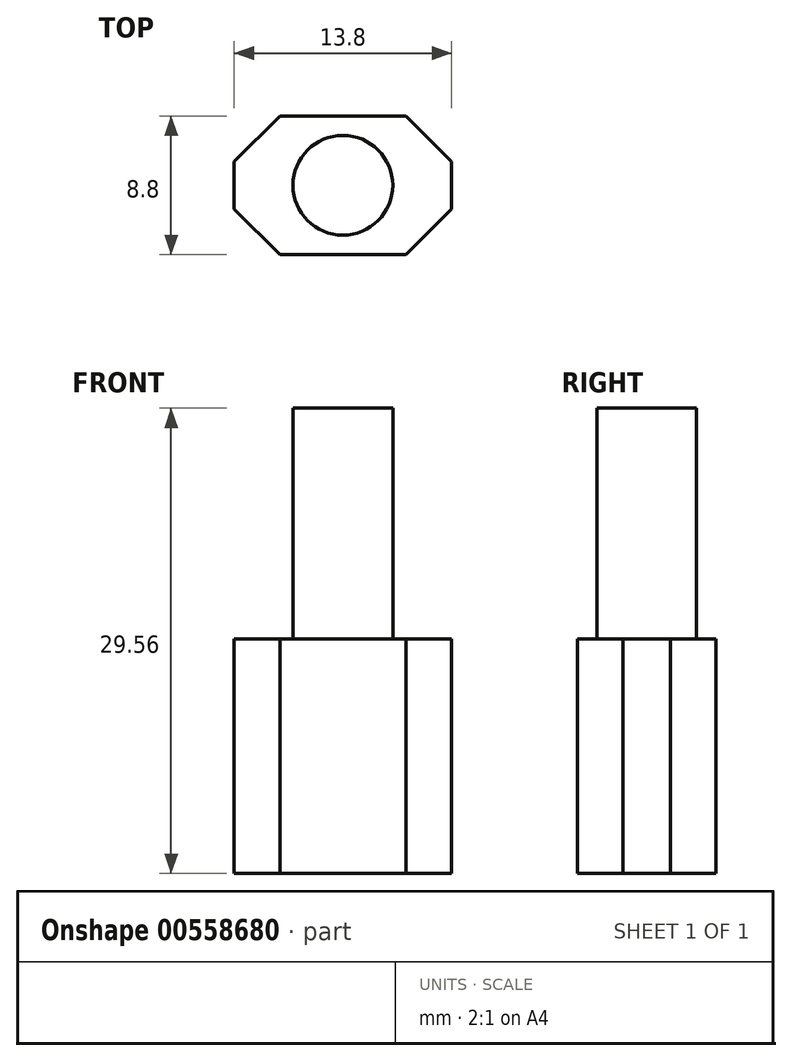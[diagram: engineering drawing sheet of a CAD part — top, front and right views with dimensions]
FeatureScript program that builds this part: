
annotation { "Feature Type Name" : "Feature", "Feature Type Description" : "" }
export const myFeature = defineFeature(function(context is Context, id is Id, definition is map)
    precondition{}
    {
        {
            var Q0;
            Q0=qCreatedBy(makeId("Top.planeOp"),FACE);
            var sketch = newSketch(context, id + "F0", { "sketchPlane" : qUnion([Q0])});
            skLineSegment(sketch, "E0", {"start": v(0, 0) * mm, "end": v(0, -4.4) * mm});
            skLineSegment(sketch, "E1", {"start": v(0, -4.4) * mm, "end": v(-4, -4.4) * mm});
            skLineSegment(sketch, "E2", {"start": v(0, -4.4) * mm, "end": v(4, -4.4) * mm});
            skLineSegment(sketch, "E3", {"start": v(6.9, -1.5) * mm, "end": v(6.9, 1.5) * mm});
            skLineSegment(sketch, "E4", {"start": v(4, 4.4) * mm, "end": v(-4, 4.4) * mm});
            skLineSegment(sketch, "E5", {"start": v(-6.9, 1.5) * mm, "end": v(-6.9, -1.5) * mm});
            skPoint(sketch, "E6.start.orphan", {"position": v(-6.9, 4.4) * mm});
            skPoint(sketch, "E7.end.orphan", {"position": v(-6.9, -4.4) * mm});
            skLineSegment(sketch, "E8", {"start": v(6.9, 1.5) * mm, "end": v(4, 4.4) * mm});
            skPoint(sketch, "E9.orphan", {"position": v(5, 4.4) * mm});
            skLineSegment(sketch, "E10", {"start": v(6.9, -1.5) * mm, "end": v(4, -4.4) * mm});
            skPoint(sketch, "E11.orphan", {"position": v(5, -4.4) * mm});
            skLineSegment(sketch, "E12", {"start": v(-6.9, 1.5) * mm, "end": v(-4, 4.4) * mm});
            skPoint(sketch, "E13.orphan", {"position": v(-5, 4.4) * mm});
            skLineSegment(sketch, "E14", {"start": v(-6.9, -1.5) * mm, "end": v(-4, -4.4) * mm});
            skPoint(sketch, "E15.orphan", {"position": v(-5, -4.4) * mm});
            skSolve(sketch);
        }
        {
            var Q0;
            Q0 = qSketchRegion(id + "F0", true);
            extrude(context, id + "F1", {"entities" : qUnion([Q0]), "depth" : 14.9 * mm, "offsetDistance" : 25 * mm});
        }
        {
            var Q0;
            Q0=makeQuery(id+"F1.opExtrude","CAP_FACE",FACE,{"disambiguationData":[OSD([sQuery(id+"F0.wireOp",EDGE,"E1"),sQuery(id+"F0.wireOp",EDGE,"E2"),sQuery(id+"F0.wireOp",EDGE,"E3"),sQuery(id+"F0.wireOp",EDGE,"E4"),sQuery(id+"F0.wireOp",EDGE,"E5"),sQuery(id+"F0.wireOp",EDGE,"XyIpxaD7-uW5D-LFlY-5q06-bDPJWgvC1OJt"),sQuery(id+"F0.wireOp",EDGE,"C9alrs6u-1IMs-B3uu-QiqS-Zq0bGt0sdqNv"),sQuery(id+"F0.wireOp",EDGE,"DIRD6rM2-hMSi-rIzV-l2VT-wHvJOkUmWRdo"),sQuery(id+"F0.wireOp",EDGE,"LL7PWqgf-2m20-zhqm-QZ33-4FFZ1Z1QkZ76")])],"isStart":false});
            var sketch = newSketch(context, id + "F2", { "sketchPlane" : qUnion([Q0])});
            skCircle(sketch, "E16", {"center": v(0, 0) * mm, "radius": 3.17 * mm});
            skLineSegment(sketch, "E17", {"start": v(0, 0) * mm, "end": v(0, -0.75) * mm});
            skLineSegment(sketch, "E18", {"start": v(0, -0.75) * mm, "end": v(-3.08, -0.75) * mm});
            skLineSegment(sketch, "E19", {"start": v(0, -0.75) * mm, "end": v(3.08, -0.75) * mm});
            skSolve(sketch);
        }
        {
            var Q0;
            Q0 = qSketchRegion(id + "F2", true);
            extrude(context, id + "F3", {"entities" : qUnion([Q0]), "operationType" : NewBodyOperationType.ADD, "depth" : 14.66 * mm, "offsetDistance" : 25 * mm});
        }
    });
